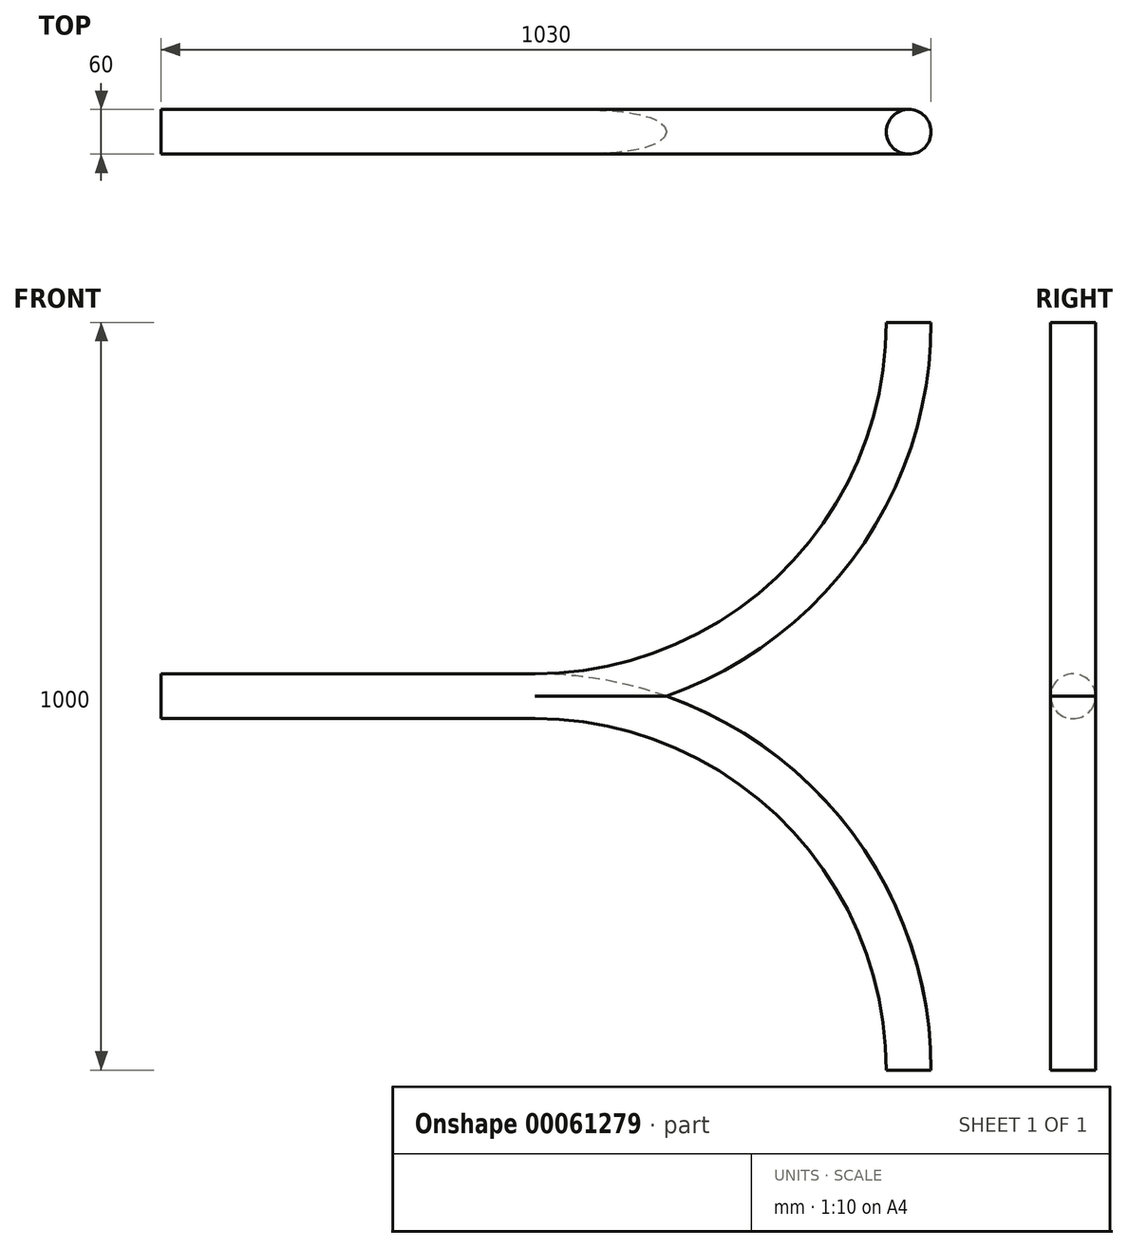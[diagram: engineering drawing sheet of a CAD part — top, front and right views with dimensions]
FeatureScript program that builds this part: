
annotation { "Feature Type Name" : "Feature", "Feature Type Description" : "" }
export const myFeature = defineFeature(function(context is Context, id is Id, definition is map)
    precondition{}
    {
        {
            var Q0;
            Q0=qCreatedBy(makeId("Front.planeOp"),FACE);
            var sketch = newSketch(context, id + "F0", { "sketchPlane" : qUnion([Q0])});
            skArc(sketch, "E0", {"start": v(0, 0) * mm, "mid": v(353.55, -146.45) * mm, "end": v(500, -500) * mm});
            skArc(sketch, "E1", {"start": v(0, 0) * mm, "mid": v(353.55, 146.45) * mm, "end": v(500, 500) * mm});
            skLineSegment(sketch, "E2", {"start": v(0, 0) * mm, "end": v(-500, 0) * mm});
            skSolve(sketch);
        }
        {
            var Q0;
            Q0=qCreatedBy(makeId("Right.planeOp"),FACE);
            var sketch = newSketch(context, id + "F1", { "sketchPlane" : qUnion([Q0])});
            skCircle(sketch, "E3", {"center": v(0, 0) * mm, "radius": 30 * mm});
            skSolve(sketch);
        }
        {
            var Q0;
            Q0=makeQuery(id+"F1.imprint","IMPRINT",FACE,{"disambiguationData":[TD([[makeQuery(id+"F1.imprint","IMPRINT",EDGE,{"derivedFrom":sQuery(id+"F1.wireOp",EDGE,"E3")}),1.0]])]});
            var Q1;
            Q1=sQuery(id+"F0.wireOp",EDGE,"E2");
            var Q2;
            Q2=sQuery(id+"F0.wireOp",EDGE,"E1");
            sweep(context, id + "F2", {"profiles" : qUnion([Q0]), "path" : qUnion([Q1, Q2])});
        }
        {
            var Q0;
            Q0 = qSketchRegion(id + "F1", true);
            var Q1;
            Q1=sQuery(id+"F0.wireOp",EDGE,"E0");
            sweep(context, id + "F3", {"operationType" : NewBodyOperationType.ADD, "profiles" : qUnion([Q0]), "path" : qUnion([Q1])});
        }
    });
